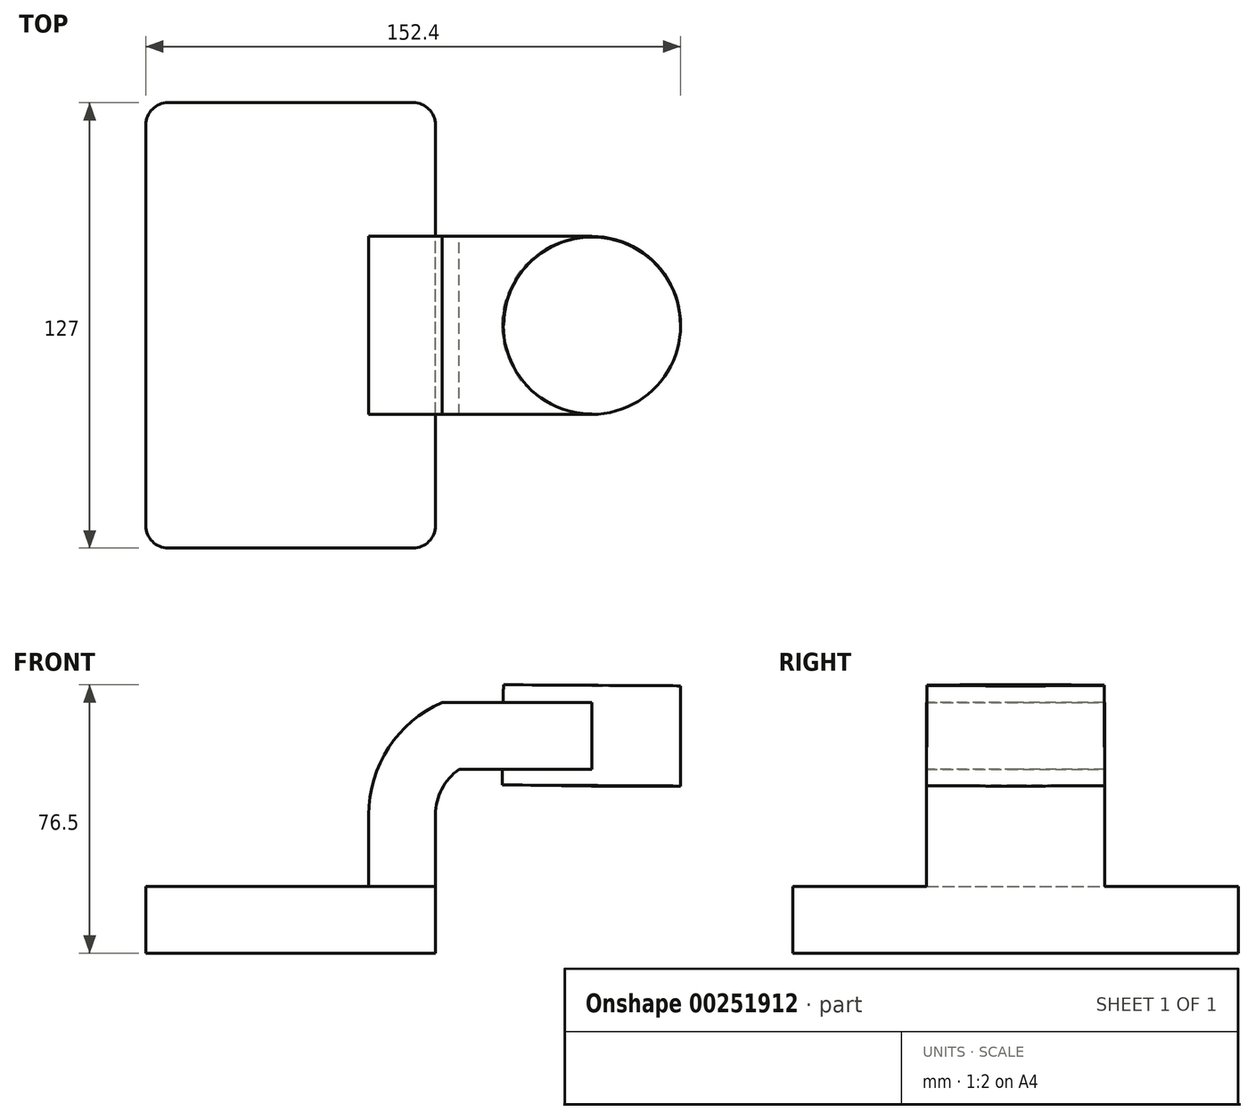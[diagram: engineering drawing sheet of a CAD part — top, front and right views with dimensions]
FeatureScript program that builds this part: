
annotation { "Feature Type Name" : "Feature", "Feature Type Description" : "" }
export const myFeature = defineFeature(function(context is Context, id is Id, definition is map)
    precondition{}
    {
        {
            var Q0;
            Q0=qCreatedBy(makeId("Front.planeOp"),FACE);
            var sketch = newSketch(context, id + "F0", { "sketchPlane" : qUnion([Q0])});
            skLineSegment(sketch, "E0.bottom", {"start": v(41.27, 9.53) * mm, "end": v(-41.28, 9.53) * mm});
            skLineSegment(sketch, "E0.top", {"start": v(41.28, -9.52) * mm, "end": v(-41.27, -9.52) * mm});
            skLineSegment(sketch, "E0.left", {"start": v(41.28, 9.53) * mm, "end": v(41.28, -9.52) * mm});
            skLineSegment(sketch, "E0.right", {"start": v(-41.28, 9.53) * mm, "end": v(-41.27, -9.52) * mm});
            skPoint(sketch, "E0.middle", {"position": v(0, 0) * mm});
            skLineSegment(sketch, "E1.bottom", {"start": v(60.33, 66.68) * mm, "end": v(111.13, 66.68) * mm});
            skLineSegment(sketch, "E1.top", {"start": v(60.33, 38.1) * mm, "end": v(111.13, 38.1) * mm});
            skLineSegment(sketch, "E1.left", {"start": v(60.33, 66.68) * mm, "end": v(60.33, 38.1) * mm});
            skLineSegment(sketch, "E1.right", {"start": v(111.13, 66.68) * mm, "end": v(111.13, 38.1) * mm});
            skPoint(sketch, "E1.middle", {"position": v(85.73, 52.39) * mm});
            skLineSegment(sketch, "E2", {"start": v(41.27, 9.53) * mm, "end": v(41.27, 29.92) * mm});
            skArc(sketch, "E3", {"start": v(41.27, 29.92) * mm, "mid": v(43.05, 37.21) * mm, "end": v(47.97, 42.88) * mm});
            skLineSegment(sketch, "E4", {"start": v(47.97, 42.88) * mm, "end": v(85.9, 42.88) * mm});
            skLineSegment(sketch, "E5.0", {"start": v(43.17, 61.93) * mm, "end": v(85.9, 61.93) * mm});
            skArc(sketch, "E5.1", {"start": v(22.23, 29.92) * mm, "mid": v(27.93, 49.04) * mm, "end": v(43.17, 61.93) * mm});
            skLineSegment(sketch, "E5.2", {"start": v(22.23, 9.53) * mm, "end": v(22.23, 29.92) * mm});
            skLineSegment(sketch, "E6", {"start": v(85.9, 61.93) * mm, "end": v(85.9, 42.88) * mm});
            skFitSpline(sketch, "E7", {"points": [v(-41.28, 9.53) * mm, v(43.17, 61.93) * mm], "startDerivative": vector(4.56, 107.52) * mm, "endDerivative": vector(111.1, 13.48) * mm});
            skLineSegment(sketch, "E8", {"start": v(85.73, 38.1) * mm, "end": v(85.9, 66.68) * mm});
            skSolve(sketch);
        }
        {
            var Q0;
            Q0=makeQuery(id+"F0.imprint","IMPRINT",FACE,{"disambiguationData":[TD([[makeQuery(id+"F0.imprint","IMPRINT",EDGE,{"derivedFrom":sQuery(id+"F0.wireOp",EDGE,"E0.top")}),-1.0]])]});
            extrude(context, id + "F1", {"entities" : qUnion([Q0]), "endBound" : BoundingType.SYMMETRIC, "depth" : 127 * mm});
        }
        {
            var Q0;
            {var subQ1=sQuery(id+"F0.wireOp",EDGE,"E2");Q0=makeQuery(id+"F0.imprint","IMPRINT",FACE,{"disambiguationData":[TD([[makeQuery(id+"F0.imprint","IMPRINT",EDGE,{"derivedFrom":subQ1}),1.0]])]});}
            var Q1;
            {var subQ5=sQuery(id+"F0.wireOp",EDGE,"E6");Q1=makeQuery(id+"F0.imprint","IMPRINT",FACE,{"disambiguationData":[TD([[makeQuery(id+"F0.imprint","IMPRINT",EDGE,{"derivedFrom":subQ5}),-1.0]])]});}
            var Q2;
            {var subQ0=sQuery(id+"F0.wireOp",EDGE,"E5.0");var subQ1=sQuery(id+"F0.wireOp",EDGE,"E1.left");var subQ2=makeQuery(id+"F0.imprint","INTERSECT",VERTEX,{"derivedFrom":[subQ1,subQ0]});Q2=makeQuery(id+"F0.imprint","IMPRINT",FACE,{"disambiguationData":[TD([[makeQuery(id+"F0.imprint","IMPRINT",EDGE,{"disambiguationData":[TD([[subQ2,-1.0]])],"derivedFrom":subQ1}),1.0]])]});}
            extrude(context, id + "F2", {"entities" : qUnion([Q0, Q1, Q2]), "operationType" : NewBodyOperationType.ADD, "endBound" : BoundingType.SYMMETRIC, "depth" : 50.8 * mm});
        }
        {
            var Q0;
            Q0=makeQuery(id+"F0.imprint","IMPRINT",FACE,{"disambiguationData":[TD([[makeQuery(id+"F0.imprint","IMPRINT",EDGE,{"derivedFrom":sQuery(id+"F0.wireOp",EDGE,"E5.1")}),1.0]])]});
            extrude(context, id + "F3", {"entities" : qUnion([Q0]), "operationType" : NewBodyOperationType.ADD, "endBound" : BoundingType.SYMMETRIC, "depth" : 15.88 * mm});
        }
        {
            var Q0;
            {var subQ4=sQuery(id+"F0.wireOp",EDGE,"E1.right");Q0=makeQuery(id+"F0.imprint","IMPRINT",FACE,{"disambiguationData":[TD([[makeQuery(id+"F0.imprint","IMPRINT",EDGE,{"derivedFrom":subQ4}),-1.0]])]});}
            var Q1;
            Q1=sQuery(id+"F0.wireOp",EDGE,"E8");
            revolve(context, id + "F4", {"operationType" : NewBodyOperationType.ADD, "entities" : qUnion([Q0]), "axis" : qUnion([Q1]), "revolveType" : RevolveType.FULL});
        }
        {
            var Q0;
            Q0=makeQuery(id+"F1.opExtrude","CAP_EDGE",EDGE,{"disambiguationData":[OSD([sQuery(id+"F0.wireOp",EDGE,"E0.right")])],"isStart":false});
            var Q1;
            Q1=makeQuery(id+"F1.opExtrude","CAP_EDGE",EDGE,{"disambiguationData":[OSD([sQuery(id+"F0.wireOp",EDGE,"E0.left")])],"isStart":false});
            var Q2;
            Q2=makeQuery(id+"F1.opExtrude","CAP_EDGE",EDGE,{"disambiguationData":[OSD([sQuery(id+"F0.wireOp",EDGE,"E0.right")])],"isStart":true});
            var Q3;
            Q3=makeQuery(id+"F1.opExtrude","CAP_EDGE",EDGE,{"disambiguationData":[OSD([sQuery(id+"F0.wireOp",EDGE,"E0.left")])],"isStart":true});
            fillet(context, id + "F5", {"entities" : qUnion([Q0, Q1, Q2, Q3]), "radius" : 6.35 * mm, "tangentPropagation" : true, "allowEdgeOverflow" : false});
        }
    });
